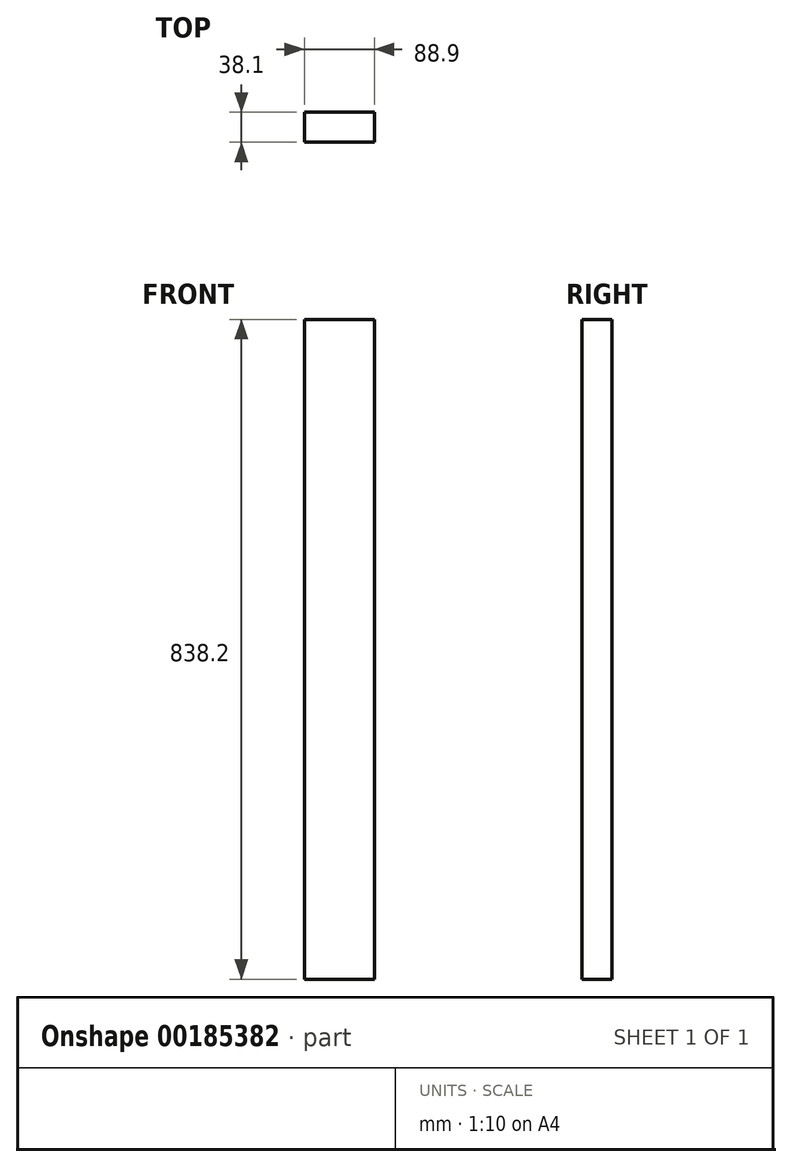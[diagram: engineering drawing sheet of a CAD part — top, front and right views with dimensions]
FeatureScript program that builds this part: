
annotation { "Feature Type Name" : "Feature", "Feature Type Description" : "" }
export const myFeature = defineFeature(function(context is Context, id is Id, definition is map)
    precondition{}
    {
        {
            var Q0;
            Q0=qCreatedBy(makeId("Top.planeOp"),FACE);
            var sketch = newSketch(context, id + "F0", { "sketchPlane" : qUnion([Q0])});
            skLineSegment(sketch, "E0.bottom", {"start": v(0, 0) * mm, "end": v(88.9, 0) * mm});
            skLineSegment(sketch, "E0.top", {"start": v(0, 38.1) * mm, "end": v(88.9, 38.1) * mm});
            skLineSegment(sketch, "E0.left", {"start": v(0, 0) * mm, "end": v(0, 38.1) * mm});
            skLineSegment(sketch, "E0.right", {"start": v(88.9, 0) * mm, "end": v(88.9, 38.1) * mm});
            skSolve(sketch);
        }
        {
            var Q0;
            Q0=makeQuery(id+"F0.imprint","IMPRINT",FACE,{"disambiguationData":[TD([[makeQuery(id+"F0.imprint","IMPRINT",EDGE,{"derivedFrom":sQuery(id+"F0.wireOp",EDGE,"E0.bottom")}),1.0]])]});
            extrude(context, id + "F1", {"entities" : qUnion([Q0]), "depth" : 838.2 * mm});
        }
    });
